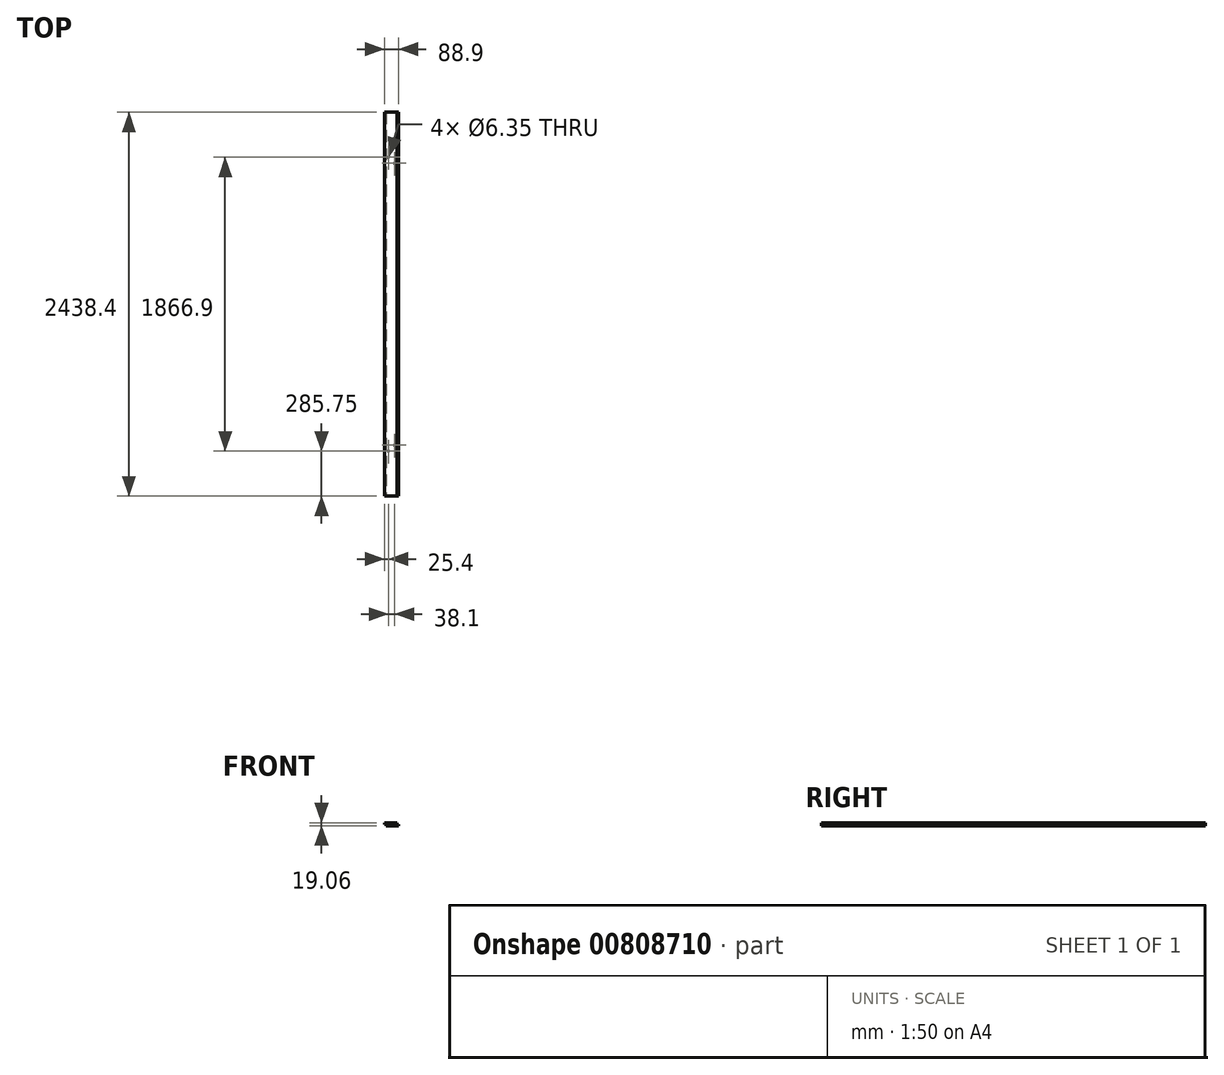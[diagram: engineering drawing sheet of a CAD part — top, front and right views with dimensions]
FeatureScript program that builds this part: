
annotation { "Feature Type Name" : "Feature", "Feature Type Description" : "" }
export const myFeature = defineFeature(function(context is Context, id is Id, definition is map)
    precondition{}
    {
        {
            var Q0;
            Q0=qCreatedBy(makeId("Front.planeOp"),FACE);
            var sketch = newSketch(context, id + "F0", { "sketchPlane" : qUnion([Q0])});
            skLineSegment(sketch, "E0.bottom", {"start": v(-44.45, 9.52) * mm, "end": v(44.45, 9.52) * mm});
            skLineSegment(sketch, "E0.top", {"start": v(-44.45, -9.52) * mm, "end": v(44.45, -9.52) * mm});
            skLineSegment(sketch, "E0.left", {"start": v(-44.45, 9.52) * mm, "end": v(-44.45, -9.53) * mm});
            skLineSegment(sketch, "E0.right", {"start": v(44.45, 9.52) * mm, "end": v(44.45, -9.53) * mm});
            skLineSegment(sketch, "E1", {"start": v(-44.45, -9.53) * mm, "end": v(44.45, 9.53) * mm, "construction": true});
            skSolve(sketch);
        }
        {
            var Q0;
            Q0 = qSketchRegion(id + "F0", true);
            extrude(context, id + "F1", {"entities" : qUnion([Q0]), "depth" : 2438.4 * mm, "offsetDistance" : 25.4 * mm, "symmetric" : true});
        }
        {
            var Q0;
            Q0=makeQuery(id+"F1.opExtrude","CAP_FACE",FACE,{"disambiguationData":[OSD([sQuery(id+"F0.wireOp",EDGE,"E0.bottom"),sQuery(id+"F0.wireOp",EDGE,"E0.top"),sQuery(id+"F0.wireOp",EDGE,"E0.left"),sQuery(id+"F0.wireOp",EDGE,"E0.right")])],"isStart":false});
            var sketch = newSketch(context, id + "F2", { "sketchPlane" : qUnion([Q0])});
            skLineSegment(sketch, "E2.bottom", {"start": v(-82.02, 0) * mm, "end": v(-34.92, 0) * mm});
            skLineSegment(sketch, "E2.top", {"start": v(-82.02, -23.13) * mm, "end": v(-34.92, -23.13) * mm});
            skLineSegment(sketch, "E2.left", {"start": v(-82.02, 0) * mm, "end": v(-82.02, -23.13) * mm});
            skLineSegment(sketch, "E2.right", {"start": v(-34.92, 0) * mm, "end": v(-34.92, -23.13) * mm});
            skLineSegment(sketch, "E3.bottom", {"start": v(34.93, 22) * mm, "end": v(79.08, 22) * mm});
            skLineSegment(sketch, "E3.top", {"start": v(34.93, 0) * mm, "end": v(79.08, 0) * mm});
            skLineSegment(sketch, "E3.left", {"start": v(34.93, 22) * mm, "end": v(34.93, 0) * mm});
            skLineSegment(sketch, "E3.right", {"start": v(79.08, 22) * mm, "end": v(79.08, 0) * mm});
            skSolve(sketch);
        }
        {
            var Q0;
            Q0 = qSketchRegion(id + "F2", true);
            extrude(context, id + "F3", {"entities" : qUnion([Q0]), "operationType" : NewBodyOperationType.REMOVE, "endBound" : BoundingType.THROUGH_ALL, "oppositeDirection" : true, "depth" : 25.4 * mm, "offsetDistance" : 25.4 * mm});
        }
        {
            var Q0;
            Q0=makeQuery(id+"F1.opExtrude","SWEPT_FACE",FACE,{"disambiguationData":[OSD([sQuery(id+"F0.wireOp",EDGE,"E0.bottom")])]});
            var sketch = newSketch(context, id + "F4", { "sketchPlane" : qUnion([Q0])});
            skLineSegment(sketch, "E4", {"start": v(0, 0) * mm, "end": v(0, -914.4) * mm, "construction": true});
            skLineSegment(sketch, "E5", {"start": v(-19.05, -914.4) * mm, "end": v(19.05, -914.4) * mm, "construction": true});
            skLineSegment(sketch, "E6.bottom", {"start": v(-19.05, -895.35) * mm, "end": v(19.05, -895.35) * mm, "construction": true});
            skLineSegment(sketch, "E6.top", {"start": v(-19.05, -933.45) * mm, "end": v(19.05, -933.45) * mm, "construction": true});
            skLineSegment(sketch, "E6.left", {"start": v(-19.05, -895.35) * mm, "end": v(-19.05, -933.45) * mm, "construction": true});
            skLineSegment(sketch, "E6.right", {"start": v(19.05, -895.35) * mm, "end": v(19.05, -933.45) * mm, "construction": true});
            skCircle(sketch, "E7", {"center": v(-19.05, -933.45) * mm, "radius": 3.18 * mm});
            skCircle(sketch, "E8", {"center": v(19.05, -895.35) * mm, "radius": 3.18 * mm});
            skLineSegment(sketch, "E9", {"start": v(0, 0) * mm, "end": v(61.5, 0) * mm, "construction": true});
            skPoint(sketch, "E9.endSnap0", {"position": v(34.93, 0) * mm});
            skCircle(sketch, "E10.MirrorC", {"center": v(-19.05, 933.45) * mm, "radius": 3.18 * mm});
            skCircle(sketch, "E11.MirrorC", {"center": v(19.05, 895.35) * mm, "radius": 3.18 * mm});
            skSolve(sketch);
        }
        {
            var Q0;
            Q0 = qSketchRegion(id + "F4", true);
            extrude(context, id + "F5", {"entities" : qUnion([Q0]), "operationType" : NewBodyOperationType.REMOVE, "endBound" : BoundingType.THROUGH_ALL, "oppositeDirection" : true, "depth" : 25.4 * mm, "offsetDistance" : 25.4 * mm});
        }
    });
